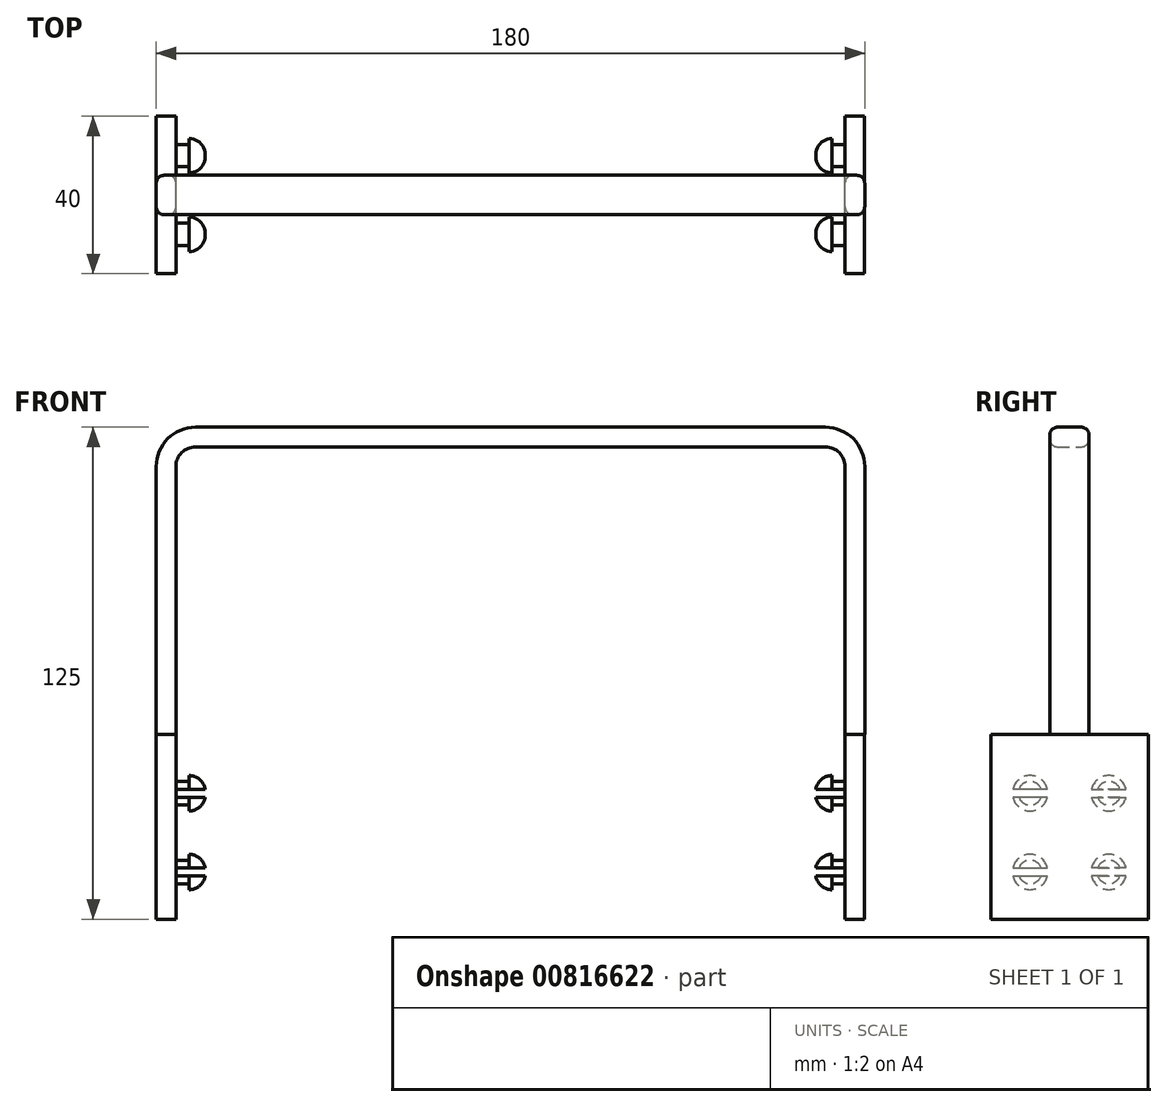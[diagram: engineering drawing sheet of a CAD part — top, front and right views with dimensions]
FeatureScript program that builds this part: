
annotation { "Feature Type Name" : "Feature", "Feature Type Description" : "" }
export const myFeature = defineFeature(function(context is Context, id is Id, definition is map)
    precondition{}
    {
        {
            var Q0;
            Q0=qCreatedBy(makeId("Front.planeOp"),FACE);
            var sketch = newSketch(context, id + "F0", { "sketchPlane" : qUnion([Q0])});
            skLineSegment(sketch, "E0", {"start": v(0, 78) * mm, "end": v(-80, 78) * mm});
            skLineSegment(sketch, "E1", {"start": v(-90, 68) * mm, "end": v(-90, 0) * mm});
            skLineSegment(sketch, "E2", {"start": v(-90, 0) * mm, "end": v(-85, 0) * mm});
            skLineSegment(sketch, "E3", {"start": v(-85, 0) * mm, "end": v(-85, 68) * mm});
            skLineSegment(sketch, "E4", {"start": v(-80, 73) * mm, "end": v(0, 73) * mm});
            skLineSegment(sketch, "E5", {"start": v(0, 98.55) * mm, "end": v(0, -22.25) * mm, "construction": true});
            skPoint(sketch, "E6.visualSharp", {"position": v(-85, 73) * mm});
            skArc(sketch, "E6.filletArc", {"start": v(-80, 73) * mm, "mid": v(-83.54, 71.54) * mm, "end": v(-85, 68) * mm});
            skPoint(sketch, "E7.visualSharp", {"position": v(-90, 78) * mm});
            skArc(sketch, "E7.filletArc", {"start": v(-80, 78) * mm, "mid": v(-87.07, 75.07) * mm, "end": v(-90, 68) * mm});
            skLineSegment(sketch, "E8.MirrorCS", {"start": v(90, 0) * mm, "end": v(85, 0) * mm});
            skArc(sketch, "E9.MirrorCS", {"start": v(80, 78) * mm, "mid": v(87.07, 75.07) * mm, "end": v(90, 68) * mm});
            skLineSegment(sketch, "E10.MirrorCS", {"start": v(0, 78) * mm, "end": v(80, 78) * mm});
            skPoint(sketch, "E11.MirrorP", {"position": v(90, 78) * mm});
            skLineSegment(sketch, "E12.MirrorCS", {"start": v(90, 68) * mm, "end": v(90, 0) * mm});
            skLineSegment(sketch, "E13.MirrorCS", {"start": v(85, 0) * mm, "end": v(85, 68) * mm});
            skPoint(sketch, "E14.MirrorP", {"position": v(85, 73) * mm});
            skArc(sketch, "E15.MirrorCS", {"start": v(80, 73) * mm, "mid": v(83.54, 71.54) * mm, "end": v(85, 68) * mm});
            skLineSegment(sketch, "E16.MirrorCS", {"start": v(80, 73) * mm, "end": v(0, 73) * mm});
            skSolve(sketch);
        }
        {
            var Q0;
            Q0 = qSketchRegion(id + "F0", true);
            extrude(context, id + "F1", {"entities" : qUnion([Q0]), "depth" : 10 * mm, "offsetDistance" : 25 * mm});
        }
        {
            var Q0;
            Q0=makeQuery(id+"F1.opExtrude","CAP_EDGE",EDGE,{"disambiguationData":[OSD([sQuery(id+"F0.wireOp",EDGE,"E0"),sQuery(id+"F0.wireOp",EDGE,"E10.MirrorCS")])],"isStart":false});
            var Q1;
            Q1=makeQuery(id+"F1.opExtrude","CAP_EDGE",EDGE,{"disambiguationData":[OSD([sQuery(id+"F0.wireOp",EDGE,"E4"),sQuery(id+"F0.wireOp",EDGE,"E16.MirrorCS")])],"isStart":false});
            var Q2;
            Q2=makeQuery(id+"F1.opExtrude","CAP_EDGE",EDGE,{"disambiguationData":[OSD([sQuery(id+"F0.wireOp",EDGE,"E12.MirrorCS")])],"isStart":true});
            var Q3;
            Q3=makeQuery(id+"F1.opExtrude","CAP_EDGE",EDGE,{"disambiguationData":[OSD([sQuery(id+"F0.wireOp",EDGE,"E13.MirrorCS")])],"isStart":true});
            fillet(context, id + "F2", {"entities" : qUnion([Q0, Q1, Q2, Q3]), "radius" : 2 * mm, "tangentPropagation" : true, "allowEdgeOverflow" : false});
        }
        {
            var Q0;
            Q0=makeQuery(id+"F1.opExtrude","SWEPT_FACE",FACE,{"disambiguationData":[OSD([sQuery(id+"F0.wireOp",EDGE,"E2")])]});
            var sketch = newSketch(context, id + "F3", { "sketchPlane" : qUnion([Q0])});
            skPoint(sketch, "E17.oppositeSnap0", {"position": v(-84.98, 5) * mm});
            skLineSegment(sketch, "E17.bottom", {"start": v(-89.98, 25) * mm, "end": v(-84.98, 25) * mm});
            skLineSegment(sketch, "E17.top", {"start": v(-89.98, -15) * mm, "end": v(-84.98, -15) * mm});
            skLineSegment(sketch, "E17.left", {"start": v(-89.98, 25) * mm, "end": v(-89.98, -15) * mm});
            skLineSegment(sketch, "E17.right", {"start": v(-84.98, 25) * mm, "end": v(-84.98, -15) * mm});
            skLineSegment(sketch, "E18", {"start": v(0, 36.49) * mm, "end": v(0, -20.35) * mm, "construction": true});
            skLineSegment(sketch, "E19.MirrorCS", {"start": v(89.98, 25) * mm, "end": v(84.98, 25) * mm});
            skLineSegment(sketch, "E20.MirrorCS", {"start": v(89.98, -15) * mm, "end": v(84.98, -15) * mm});
            skPoint(sketch, "E21.MirrorP", {"position": v(84.98, 5) * mm});
            skLineSegment(sketch, "E22.MirrorCS", {"start": v(89.98, 25) * mm, "end": v(89.98, -15) * mm});
            skLineSegment(sketch, "E23.MirrorCS", {"start": v(84.98, 25) * mm, "end": v(84.98, -15) * mm});
            skSolve(sketch);
        }
        {
            var Q0;
            Q0 = qSketchRegion(id + "F3", true);
            extrude(context, id + "F4", {"entities" : qUnion([Q0]), "operationType" : NewBodyOperationType.ADD, "depth" : 47 * mm, "offsetDistance" : 25 * mm});
        }
        {
            var Q0;
            Q0=makeQuery(id+"F4.opExtrude","SWEPT_FACE",FACE,{"disambiguationData":[OSD([sQuery(id+"F3.wireOp",EDGE,"E17.left")])]});
            var sketch = newSketch(context, id + "F5", { "sketchPlane" : qUnion([Q0])});
            skLineSegment(sketch, "E24", {"start": v(5, 10.28) * mm, "end": v(5, -104.28) * mm, "construction": true});
            skCircle(sketch, "E25", {"center": v(15, -15) * mm, "radius": 3 * mm});
            skCircle(sketch, "E26", {"center": v(-5, -35) * mm, "radius": 3 * mm});
            skSolve(sketch);
        }
        {
            var Q0;
            Q0 = qSketchRegion(id + "F5", true);
            extrude(context, id + "F6", {"entities" : qUnion([Q0]), "operationType" : NewBodyOperationType.ADD, "oppositeDirection" : true, "depth" : 8.3 * mm, "offsetDistance" : 25 * mm});
        }
        {
            var Q0;
            Q0=makeQuery(id+"F4.opExtrude","SWEPT_FACE",FACE,{"disambiguationData":[OSD([sQuery(id+"F3.wireOp",EDGE,"E22.MirrorCS")])]});
            var sketch = newSketch(context, id + "F7", { "sketchPlane" : qUnion([Q0])});
            skLineSegment(sketch, "E27", {"start": v(-5, 8.5) * mm, "end": v(-5, -102.5) * mm, "construction": true});
            skPoint(sketch, "E28", {"position": v(-5, 0) * mm});
            skCircle(sketch, "E29", {"center": v(5, -15) * mm, "radius": 3 * mm});
            skCircle(sketch, "E30", {"center": v(-15, -35) * mm, "radius": 3 * mm});
            skSolve(sketch);
        }
        {
            var Q0;
            Q0 = qSketchRegion(id + "F7", true);
            extrude(context, id + "F8", {"entities" : qUnion([Q0]), "operationType" : NewBodyOperationType.ADD, "oppositeDirection" : true, "depth" : 8.3 * mm, "offsetDistance" : 25 * mm});
        }
        {
            var Q0;
            Q0=makeQuery(id+"F8.opExtrude","CAP_FACE",FACE,{"disambiguationData":[OSD([sQuery(id+"F7.wireOp",EDGE,"E29")])],"isStart":false});
            var sketch = newSketch(context, id + "F9", { "sketchPlane" : qUnion([Q0])});
            skCircle(sketch, "E31", {"center": v(-5, -15) * mm, "radius": 4.5 * mm});
            skCircle(sketch, "E32", {"center": v(15, -35) * mm, "radius": 4.5 * mm});
            skSolve(sketch);
        }
        {
            var Q0;
            Q0 = qSketchRegion(id + "F9", true);
            extrude(context, id + "F10", {"entities" : qUnion([Q0]), "operationType" : NewBodyOperationType.ADD, "depth" : 4.2 * mm, "offsetDistance" : 25 * mm});
        }
        {
            var Q0;
            Q0=makeQuery(id+"F10.opExtrude","CAP_EDGE",EDGE,{"disambiguationData":[OSD([sQuery(id+"F9.wireOp",EDGE,"E31")])],"isStart":false});
            var Q1;
            Q1=makeQuery(id+"F10.opExtrude","CAP_EDGE",EDGE,{"disambiguationData":[OSD([sQuery(id+"F9.wireOp",EDGE,"E32")])],"isStart":false});
            fillet(context, id + "F11", {"entities" : qUnion([Q0, Q1]), "radius" : 4.2 * mm, "tangentPropagation" : true, "allowEdgeOverflow" : false});
        }
        {
            var Q0;
            Q0=makeQuery(id+"F6.opExtrude","CAP_FACE",FACE,{"disambiguationData":[OSD([sQuery(id+"F5.wireOp",EDGE,"E25")])],"isStart":false});
            var sketch = newSketch(context, id + "F12", { "sketchPlane" : qUnion([Q0])});
            skCircle(sketch, "E33", {"center": v(-15, -15) * mm, "radius": 4.5 * mm});
            skCircle(sketch, "E34", {"center": v(5, -35) * mm, "radius": 4.5 * mm});
            skSolve(sketch);
        }
        {
            var Q0;
            Q0 = qSketchRegion(id + "F12", true);
            extrude(context, id + "F13", {"entities" : qUnion([Q0]), "operationType" : NewBodyOperationType.ADD, "depth" : 4.2 * mm, "offsetDistance" : 25 * mm});
        }
        {
            var Q0;
            Q0=makeQuery(id+"F13.opExtrude","CAP_EDGE",EDGE,{"disambiguationData":[OSD([sQuery(id+"F12.wireOp",EDGE,"E33")])],"isStart":false});
            var Q1;
            Q1=makeQuery(id+"F13.opExtrude","CAP_EDGE",EDGE,{"disambiguationData":[OSD([sQuery(id+"F12.wireOp",EDGE,"E34")])],"isStart":false});
            fillet(context, id + "F14", {"entities" : qUnion([Q0, Q1]), "radius" : 4.2 * mm, "tangentPropagation" : true, "allowEdgeOverflow" : false});
        }
        {
            var Q0;
            Q0=qCreatedBy(makeId("Top.planeOp"),FACE);
            cPlane(context, id + "F15", {"entities" : qUnion([Q0]), "cplaneType" : CPlaneType.OFFSET, "offset" : 16 * mm, "oppositeDirection" : true, "width" : 150 * mm, "height" : 150 * mm});
        }
        {
            var Q0;
            Q0=qCreatedBy(id+"F15.planeOp",FACE);
            var sketch = newSketch(context, id + "F16", { "sketchPlane" : qUnion([Q0])});
            skLineSegment(sketch, "E35.bottom", {"start": v(84.98, 11.73) * mm, "end": v(-84.98, 11.73) * mm});
            skLineSegment(sketch, "E35.top", {"start": v(84.98, -23.17) * mm, "end": v(-84.98, -23.17) * mm});
            skLineSegment(sketch, "E35.left", {"start": v(84.98, 11.73) * mm, "end": v(84.98, -23.17) * mm});
            skLineSegment(sketch, "E35.right", {"start": v(-84.98, 11.73) * mm, "end": v(-84.98, -23.17) * mm});
            skSolve(sketch);
        }
        {
            var Q0;
            Q0 = qSketchRegion(id + "F16", true);
            extrude(context, id + "F17", {"entities" : qUnion([Q0]), "operationType" : NewBodyOperationType.REMOVE, "depth" : 2 * mm, "offsetDistance" : 25 * mm});
        }
        {
            var Q0;
            Q0=qCreatedBy(makeId("Top.planeOp"),FACE);
            cPlane(context, id + "F18", {"entities" : qUnion([Q0]), "cplaneType" : CPlaneType.OFFSET, "offset" : 36 * mm, "oppositeDirection" : true, "width" : 150 * mm, "height" : 150 * mm});
        }
        {
            var Q0;
            Q0=qCreatedBy(id+"F18.planeOp",FACE);
            var sketch = newSketch(context, id + "F19", { "sketchPlane" : qUnion([Q0])});
            skLineSegment(sketch, "E36.bottom", {"start": v(-84.98, -22.32) * mm, "end": v(84.98, -22.32) * mm});
            skLineSegment(sketch, "E36.top", {"start": v(-84.98, 12.23) * mm, "end": v(84.98, 12.23) * mm});
            skLineSegment(sketch, "E36.left", {"start": v(-84.98, -22.32) * mm, "end": v(-84.98, 12.23) * mm});
            skLineSegment(sketch, "E36.right", {"start": v(84.98, -22.32) * mm, "end": v(84.98, 12.23) * mm});
            skSolve(sketch);
        }
        {
            var Q0;
            Q0 = qSketchRegion(id + "F19", true);
            extrude(context, id + "F20", {"entities" : qUnion([Q0]), "operationType" : NewBodyOperationType.REMOVE, "depth" : 2 * mm, "offsetDistance" : 25 * mm});
        }
    });
